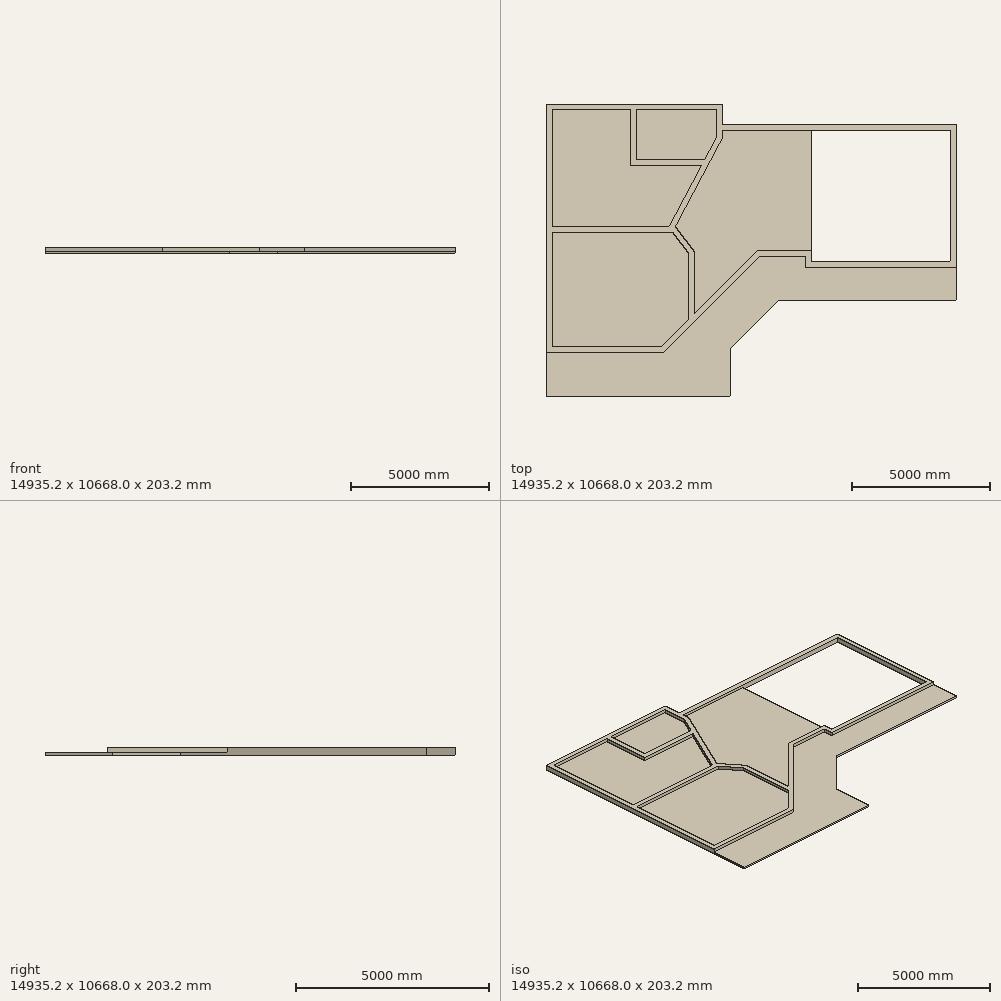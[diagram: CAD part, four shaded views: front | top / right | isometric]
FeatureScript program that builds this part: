
annotation { "Feature Type Name" : "Feature", "Feature Type Description" : "" }
export const myFeature = defineFeature(function(context is Context, id is Id, definition is map)
    precondition{}
    {
        {
            var Q0;
            Q0=qCreatedBy(makeId("Top.planeOp"),FACE);
            var sketch = newSketch(context, id + "F0", { "sketchPlane" : qUnion([Q0])});
            skLineSegment(sketch, "E0.bottom", {"start": v(0, 0) * mm, "end": v(14935.2, 0) * mm});
            skLineSegment(sketch, "E0.top", {"start": v(0, 11582.4) * mm, "end": v(14935.2, 11582.4) * mm});
            skLineSegment(sketch, "E0.left", {"start": v(0, 0) * mm, "end": v(0, 11582.4) * mm});
            skLineSegment(sketch, "E0.right", {"start": v(14935.2, 0) * mm, "end": v(14935.2, 11582.4) * mm});
            skLineSegment(sketch, "E1", {"start": v(6705.6, 0) * mm, "end": v(6705.6, 1752.6) * mm});
            skLineSegment(sketch, "E2", {"start": v(6705.6, 1752.6) * mm, "end": v(8458.2, 3505.2) * mm});
            skLineSegment(sketch, "E3", {"start": v(0, 10668) * mm, "end": v(6400.8, 10668) * mm});
            skLineSegment(sketch, "E4", {"start": v(6400.8, 10668) * mm, "end": v(6400.8, 9906) * mm});
            skLineSegment(sketch, "E5", {"start": v(6400.8, 9906) * mm, "end": v(14935.2, 9906) * mm});
            skLineSegment(sketch, "E6", {"start": v(7467.6, 11582.4) * mm, "end": v(7467.6, 10820.4) * mm});
            skLineSegment(sketch, "E7", {"start": v(7467.6, 10820.4) * mm, "end": v(14935.2, 10820.4) * mm});
            skLineSegment(sketch, "E8", {"start": v(8458.2, 3505.2) * mm, "end": v(14935.2, 3505.2) * mm});
            skSolve(sketch);
        }
        {
            var Q0;
            {var subQ7=sQuery(id+"F0.wireOp",EDGE,"E1");Q0=makeQuery(id+"F0.imprint","IMPRINT",FACE,{"disambiguationData":[TD([[makeQuery(id+"F0.imprint","IMPRINT",EDGE,{"derivedFrom":subQ7}),1.0]])]});}
            extrude(context, id + "F1", {"entities" : qUnion([Q0]), "depth" : 76.2 * mm, "offsetDistance" : 25.4 * mm});
        }
        {
            var Q0;
            Q0=makeQuery(id+"F1.opExtrude","CAP_FACE",FACE,{"disambiguationData":[OSD([sQuery(id+"F0.wireOp",EDGE,"E0.bottom"),sQuery(id+"F0.wireOp",EDGE,"E0.left"),sQuery(id+"F0.wireOp",EDGE,"E0.right"),sQuery(id+"F0.wireOp",EDGE,"E1"),sQuery(id+"F0.wireOp",EDGE,"E2"),sQuery(id+"F0.wireOp",EDGE,"E3"),sQuery(id+"F0.wireOp",EDGE,"E4"),sQuery(id+"F0.wireOp",EDGE,"E5"),sQuery(id+"F0.wireOp",EDGE,"E8")])],"isStart":false});
            var sketch = newSketch(context, id + "F2", { "sketchPlane" : qUnion([Q0])});
            skLineSegment(sketch, "E9", {"start": v(0, 10668) * mm, "end": v(0, 0) * mm});
            skLineSegment(sketch, "E10", {"start": v(0, 10668) * mm, "end": v(6400.8, 10668) * mm});
            skLineSegment(sketch, "E11", {"start": v(6400.8, 9906) * mm, "end": v(14935.2, 9906) * mm});
            skLineSegment(sketch, "E12", {"start": v(14935.2, 9906) * mm, "end": v(14935.2, 3505.2) * mm});
            skLineSegment(sketch, "E13", {"start": v(14935.2, 3505.2) * mm, "end": v(8458.2, 3505.2) * mm});
            skLineSegment(sketch, "E14", {"start": v(8458.2, 3505.2) * mm, "end": v(6705.6, 1752.6) * mm});
            skLineSegment(sketch, "E15", {"start": v(6705.6, 1752.6) * mm, "end": v(6705.6, 0) * mm});
            skLineSegment(sketch, "E16", {"start": v(6705.6, 0) * mm, "end": v(0, 0) * mm});
            skLineSegment(sketch, "E17", {"start": v(203.2, 10464.8) * mm, "end": v(203.2, 6197.6) * mm});
            skLineSegment(sketch, "E18", {"start": v(203.2, 10464.8) * mm, "end": v(3073.4, 10464.8) * mm});
            skLineSegment(sketch, "E19", {"start": v(6400.8, 9702.8) * mm, "end": v(14732, 9702.8) * mm});
            skLineSegment(sketch, "E20", {"start": v(14732, 9702.8) * mm, "end": v(14732, 4927.6) * mm});
            skLineSegment(sketch, "E21", {"start": v(203.2, 1828.8) * mm, "end": v(4195.49, 1828.8) * mm});
            skLineSegment(sketch, "E22", {"start": v(4195.49, 1828.8) * mm, "end": v(5181.9, 2815.22) * mm});
            skLineSegment(sketch, "E23", {"start": v(9652, 5334) * mm, "end": v(7700.69, 5334) * mm});
            skLineSegment(sketch, "E24", {"start": v(0, 1625.6) * mm, "end": v(4279.65, 1625.6) * mm});
            skLineSegment(sketch, "E25", {"start": v(4279.65, 1625.6) * mm, "end": v(7784.85, 5130.8) * mm});
            skLineSegment(sketch, "E26", {"start": v(7784.85, 5130.8) * mm, "end": v(9448.8, 5130.8) * mm});
            skLineSegment(sketch, "E27", {"start": v(203.2, 6197.6) * mm, "end": v(4470.4, 6197.6) * mm});
            skLineSegment(sketch, "E28", {"start": v(203.2, 5994.4) * mm, "end": v(4592.54, 5994.4) * mm});
            skLineSegment(sketch, "E29.trimOffspring", {"start": v(203.2, 5994.4) * mm, "end": v(203.2, 1828.8) * mm});
            skLineSegment(sketch, "E30", {"start": v(6197.6, 10464.8) * mm, "end": v(6197.6, 9448.8) * mm});
            skLineSegment(sketch, "E31", {"start": v(6400.8, 9702.8) * mm, "end": v(6400.8, 9398.18) * mm});
            skLineSegment(sketch, "E32", {"start": v(4470.4, 6197.6) * mm, "end": v(5657.85, 8432.8) * mm});
            skLineSegment(sketch, "E33", {"start": v(4697.22, 6191.43) * mm, "end": v(6400.8, 9398.18) * mm});
            skPoint(sketch, "E34.orphan", {"position": v(6400.8, 9093.55) * mm});
            skLineSegment(sketch, "E35", {"start": v(3276.6, 10464.8) * mm, "end": v(3276.6, 8636) * mm});
            skLineSegment(sketch, "E36", {"start": v(3276.6, 8636) * mm, "end": v(5765.8, 8636) * mm});
            skLineSegment(sketch, "E37", {"start": v(3073.4, 8432.8) * mm, "end": v(5657.85, 8432.8) * mm});
            skLineSegment(sketch, "E38", {"start": v(3073.4, 8432.8) * mm, "end": v(3073.4, 10464.8) * mm});
            skLineSegment(sketch, "E39.trimOffspring", {"start": v(5765.8, 8636) * mm, "end": v(6197.6, 9448.8) * mm});
            skLineSegment(sketch, "E40.trimOffspring", {"start": v(3276.6, 10464.8) * mm, "end": v(6197.6, 10464.8) * mm});
            skPoint(sketch, "E41.orphan", {"position": v(14732, 5130.8) * mm});
            skLineSegment(sketch, "E42", {"start": v(4592.54, 5994.4) * mm, "end": v(5181.9, 5230.03) * mm});
            skLineSegment(sketch, "E43", {"start": v(5181.9, 5230.03) * mm, "end": v(5181.9, 2815.22) * mm});
            skLineSegment(sketch, "E44", {"start": v(4697.22, 6191.43) * mm, "end": v(5385.1, 5299.27) * mm});
            skLineSegment(sketch, "E45", {"start": v(5385.1, 5299.27) * mm, "end": v(5385.1, 3018.42) * mm});
            skLineSegment(sketch, "E46.trimOffspring", {"start": v(5385.1, 3018.42) * mm, "end": v(7700.69, 5334) * mm});
            skLineSegment(sketch, "E47", {"start": v(9448.8, 5130.8) * mm, "end": v(9448.8, 4724.4) * mm});
            skLineSegment(sketch, "E48", {"start": v(9448.8, 4724.4) * mm, "end": v(14935.2, 4724.4) * mm});
            skLineSegment(sketch, "E49", {"start": v(9652, 5334) * mm, "end": v(9652, 4927.6) * mm});
            skLineSegment(sketch, "E50", {"start": v(9652, 4927.6) * mm, "end": v(14732, 4927.6) * mm});
            skPoint(sketch, "E51.orphan", {"position": v(14732, 5334) * mm});
            skSolve(sketch);
        }
        {
            var Q0;
            {var subQ3=sQuery(id+"F2.wireOp",EDGE,"E10");Q0=makeQuery(id+"F2.imprint","IMPRINT",FACE,{"disambiguationData":[TD([[makeQuery(id+"F2.imprint","IMPRINT",EDGE,{"derivedFrom":subQ3}),-1.0]])]});}
            extrude(context, id + "F3", {"entities" : qUnion([Q0]), "operationType" : NewBodyOperationType.ADD, "depth" : 127 * mm, "offsetDistance" : 25.4 * mm});
        }
        {
            var Q0;
            Q0=makeQuery(id+"F3.boolean.opBoolean","SPLIT",FACE,{"disambiguationData":[TD([makeQuery(id+"F3.opExtrude","SWEPT_FACE",FACE,{"disambiguationData":[OSD([sQuery(id+"F2.wireOp",EDGE,"E19")])]})])],"derivedFrom":makeQuery(id+"F1.opExtrude","CAP_FACE",FACE,{"disambiguationData":[OSD([sQuery(id+"F0.wireOp",EDGE,"E0.bottom"),sQuery(id+"F0.wireOp",EDGE,"E0.left"),sQuery(id+"F0.wireOp",EDGE,"E0.right"),sQuery(id+"F0.wireOp",EDGE,"E1"),sQuery(id+"F0.wireOp",EDGE,"E2"),sQuery(id+"F0.wireOp",EDGE,"E3"),sQuery(id+"F0.wireOp",EDGE,"E4"),sQuery(id+"F0.wireOp",EDGE,"E5"),sQuery(id+"F0.wireOp",EDGE,"E8")])],"isStart":false})});
            var sketch = newSketch(context, id + "F4", { "sketchPlane" : qUnion([Q0])});
            skLineSegment(sketch, "E52.bottom", {"start": v(14732, 4927.6) * mm, "end": v(9652, 4927.6) * mm});
            skLineSegment(sketch, "E52.top", {"start": v(14732, 9702.8) * mm, "end": v(9652, 9702.8) * mm});
            skLineSegment(sketch, "E52.left", {"start": v(14732, 4927.6) * mm, "end": v(14732, 9702.8) * mm});
            skLineSegment(sketch, "E52.right", {"start": v(9652, 4927.6) * mm, "end": v(9652, 9702.8) * mm});
            skSolve(sketch);
        }
        {
            var Q0;
            {var subQ3=sQuery(id+"F4.wireOp",EDGE,"E52.bottom");Q0=makeQuery(id+"F4.imprint","IMPRINT",FACE,{"disambiguationData":[TD([[makeQuery(id+"F4.imprint","IMPRINT",EDGE,{"derivedFrom":subQ3}),1.0]])]});}
            extrude(context, id + "F5", {"entities" : qUnion([Q0]), "operationType" : NewBodyOperationType.REMOVE, "oppositeDirection" : true, "depth" : 76.2 * mm, "offsetDistance" : 25.4 * mm});
        }
    });
